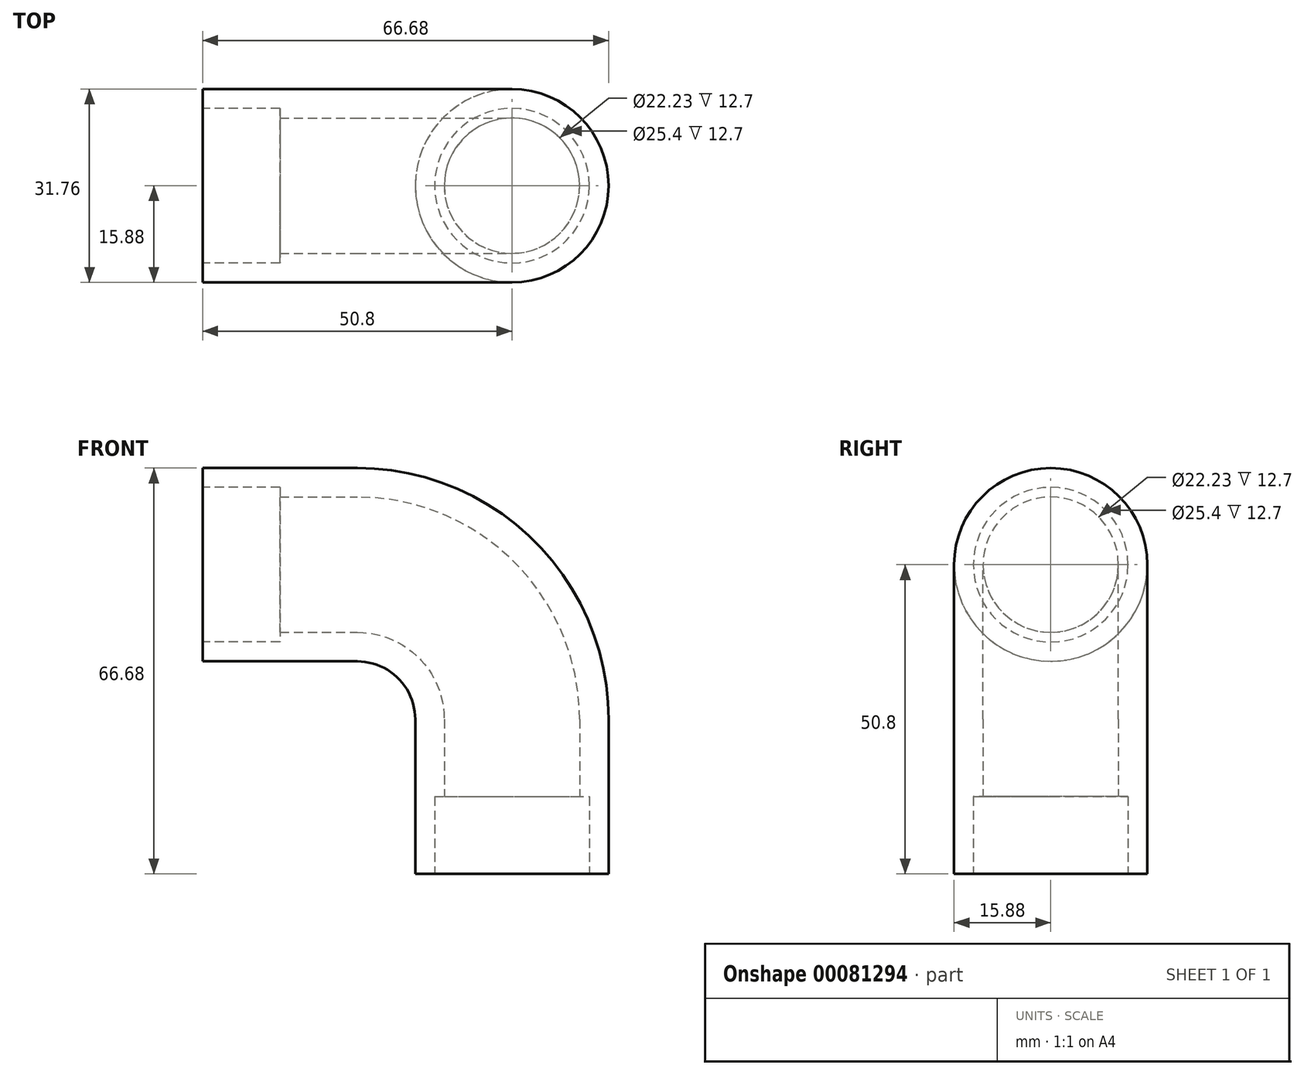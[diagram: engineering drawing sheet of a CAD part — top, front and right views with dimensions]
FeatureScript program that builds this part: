
annotation { "Feature Type Name" : "Feature", "Feature Type Description" : "" }
export const myFeature = defineFeature(function(context is Context, id is Id, definition is map)
    precondition{}
    {
        {
            var Q0;
            Q0=qCreatedBy(makeId("Right.planeOp"),FACE);
            var sketch = newSketch(context, id + "F0", { "sketchPlane" : qUnion([Q0])});
            skCircle(sketch, "E0", {"center": v(0, 0) * mm, "radius": 15.88 * mm});
            skCircle(sketch, "E1", {"center": v(0, 0) * mm, "radius": 11.11 * mm});
            skSolve(sketch);
        }
        {
            var Q0;
            Q0=qCreatedBy(makeId("Front.planeOp"),FACE);
            var sketch = newSketch(context, id + "F1", { "sketchPlane" : qUnion([Q0])});
            skLineSegment(sketch, "E2", {"start": v(0, 0) * mm, "end": v(25.4, 0) * mm});
            skLineSegment(sketch, "E3", {"start": v(50.8, -25.4) * mm, "end": v(50.8, -50.8) * mm});
            skPoint(sketch, "E4.visualSharp", {"position": v(50.8, 0) * mm});
            skArc(sketch, "E4.filletArc", {"start": v(50.8, -25.4) * mm, "mid": v(43.36, -7.44) * mm, "end": v(25.4, 0) * mm});
            skSolve(sketch);
        }
        {
            var Q0;
            Q0=makeQuery(id+"F0.imprint","IMPRINT",FACE,{"disambiguationData":[TD([[makeQuery(id+"F0.imprint","IMPRINT",EDGE,{"derivedFrom":sQuery(id+"F0.wireOp",EDGE,"E0")}),1.0]])]});
            var Q1;
            Q1=sQuery(id+"F1.wireOp",EDGE,"E2");
            var Q2;
            Q2=sQuery(id+"F1.wireOp",EDGE,"E4.filletArc");
            var Q3;
            Q3=sQuery(id+"F1.wireOp",EDGE,"E3");
            sweep(context, id + "F2", {"profiles" : qUnion([Q0]), "path" : qUnion([Q1, Q2, Q3])});
        }
        {
            var Q0;
            Q0=makeQuery(id+"F2.opSweep","CAP_FACE",FACE,{"disambiguationData":[OSD([sQuery(id+"F0.wireOp",EDGE,"E0"),sQuery(id+"F0.wireOp",EDGE,"E1"),sQuery(id+"F1.wireOp",VERTEX,"E2.start")])],"isStart":true});
            var sketch = newSketch(context, id + "F3", { "sketchPlane" : qUnion([Q0])});
            skCircle(sketch, "E5", {"center": v(0, 0) * mm, "radius": 12.7 * mm});
            skSolve(sketch);
        }
        {
            var Q0;
            Q0=makeQuery(id+"F3.imprint","IMPRINT",FACE,{"disambiguationData":[TD([[makeQuery(id+"F3.imprint","IMPRINT",EDGE,{"derivedFrom":sQuery(id+"F3.wireOp",EDGE,"E5")}),1.0]])]});
            extrude(context, id + "F4", {"entities" : qUnion([Q0]), "operationType" : NewBodyOperationType.REMOVE, "oppositeDirection" : true, "depth" : 12.7 * mm});
        }
        {
            var Q0;
            Q0=makeQuery(id+"F2.opSweep","CAP_FACE",FACE,{"disambiguationData":[OSD([sQuery(id+"F0.wireOp",EDGE,"E0"),sQuery(id+"F0.wireOp",EDGE,"E1"),sQuery(id+"F1.wireOp",VERTEX,"E3.end")])],"isStart":false});
            var sketch = newSketch(context, id + "F5", { "sketchPlane" : qUnion([Q0])});
            skCircle(sketch, "E6", {"center": v(50.8, 0) * mm, "radius": 12.7 * mm});
            skSolve(sketch);
        }
        {
            var Q0;
            Q0=makeQuery(id+"F5.imprint","IMPRINT",FACE,{"disambiguationData":[TD([[makeQuery(id+"F5.imprint","IMPRINT",EDGE,{"derivedFrom":sQuery(id+"F5.wireOp",EDGE,"E6")}),1.0]])]});
            extrude(context, id + "F6", {"entities" : qUnion([Q0]), "operationType" : NewBodyOperationType.REMOVE, "oppositeDirection" : true, "depth" : 12.7 * mm});
        }
    });
